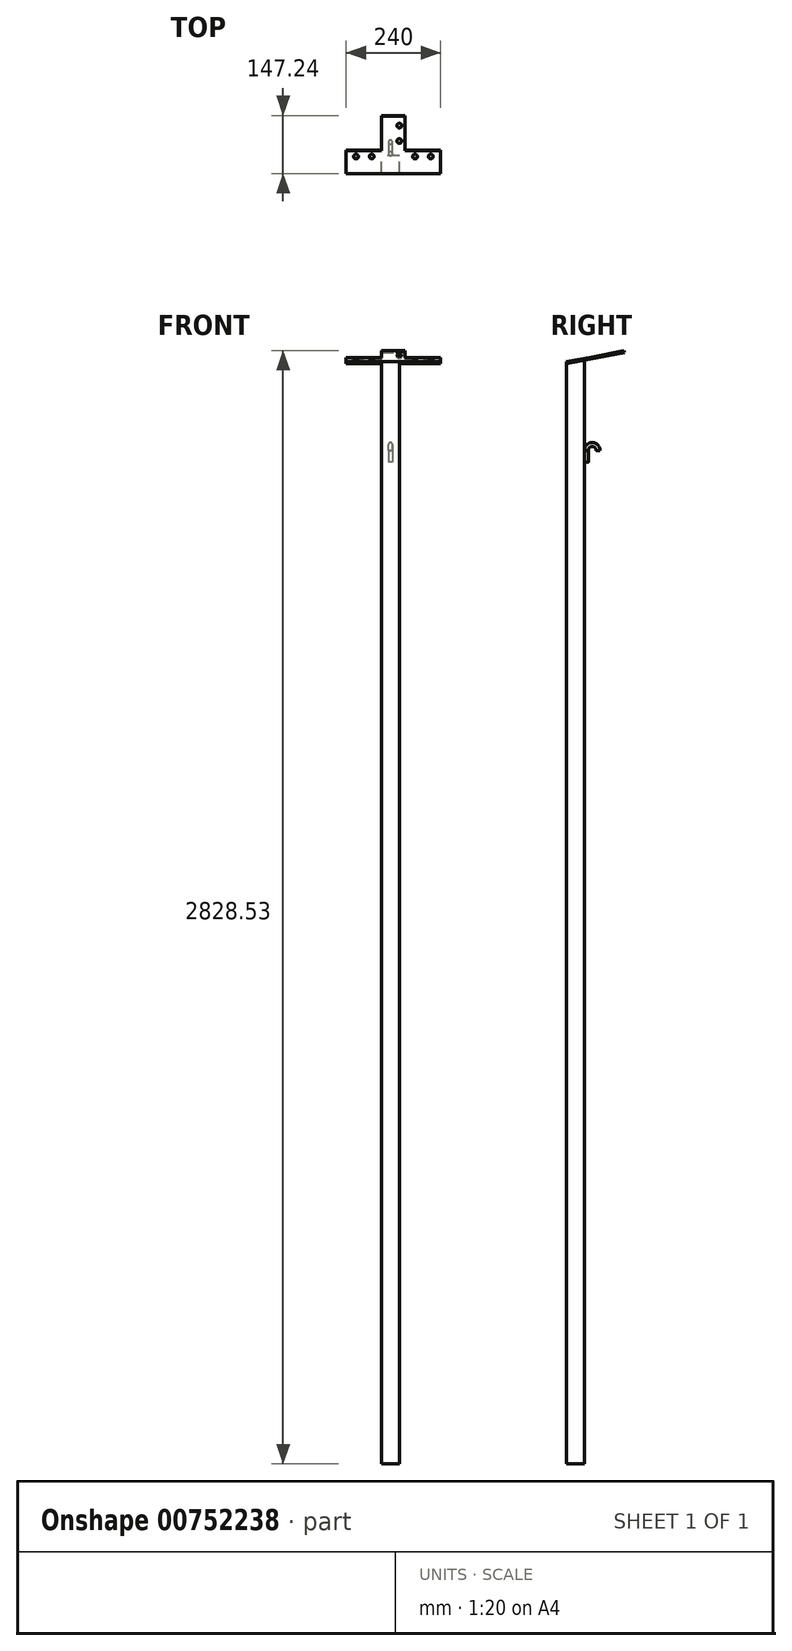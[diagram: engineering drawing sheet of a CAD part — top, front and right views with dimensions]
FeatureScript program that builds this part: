
annotation { "Feature Type Name" : "Feature", "Feature Type Description" : "" }
export const myFeature = defineFeature(function(context is Context, id is Id, definition is map)
    precondition{}
    {
        {
            var Q0;
            Q0=qCreatedBy(makeId("Top.planeOp"),FACE);
            var sketch = newSketch(context, id + "F0", { "sketchPlane" : qUnion([Q0])});
            skLineSegment(sketch, "E0.bottom", {"start": v(22.5, -22.5) * mm, "end": v(-22.5, -22.5) * mm});
            skLineSegment(sketch, "E0.top", {"start": v(22.5, 22.5) * mm, "end": v(-22.5, 22.5) * mm});
            skLineSegment(sketch, "E0.left", {"start": v(22.5, -22.5) * mm, "end": v(22.5, 22.5) * mm});
            skLineSegment(sketch, "E0.right", {"start": v(-22.5, -22.5) * mm, "end": v(-22.5, 22.5) * mm});
            skPoint(sketch, "E0.middle", {"position": v(0, 0) * mm});
            skSolve(sketch);
        }
        {
            var Q0;
            Q0=qSketchRegion(id+"F0",true);
            extrude(context, id + "F1", {"entities" : qUnion([Q0]), "depth" : 2795 * mm, "offsetDistance" : 25 * mm});
        }
        {
            var Q0;
            Q0=makeQuery(id+"F1.opExtrude","CAP_EDGE",EDGE,{"disambiguationData":[OSD([sQuery(id+"F0.wireOp",EDGE,"E0.bottom")])],"isStart":false});
            cPlane(context, id + "F2", {"entities" : qUnion([Q0]), "cplaneType" : CPlaneType.LINE_ANGLE, "offset" : 25 * mm, "angle" : 79 * degree, "width" : 150 * mm, "height" : 150 * mm});
        }
        {
            var Q0;
            Q0=qCreatedBy(id+"F2.planeOp",FACE);
            var sketch = newSketch(context, id + "F3", { "sketchPlane" : qUnion([Q0])});
            skLineSegment(sketch, "E1.bottom", {"start": v(-22.5, 511.22) * mm, "end": v(37.5, 511.22) * mm});
            skLineSegment(sketch, "E1.top", {"start": v(-22.5, 661.22) * mm, "end": v(37.5, 661.22) * mm});
            skLineSegment(sketch, "E1.left", {"start": v(-22.5, 511.22) * mm, "end": v(-22.5, 661.22) * mm});
            skLineSegment(sketch, "E1.right", {"start": v(37.5, 511.22) * mm, "end": v(37.5, 661.22) * mm});
            skLineSegment(sketch, "E2.bottom", {"start": v(37.5, 511.22) * mm, "end": v(127.5, 511.22) * mm});
            skLineSegment(sketch, "E2.top", {"start": v(37.5, 571.22) * mm, "end": v(127.5, 571.22) * mm});
            skLineSegment(sketch, "E2.left", {"start": v(37.5, 511.22) * mm, "end": v(37.5, 571.22) * mm});
            skLineSegment(sketch, "E2.right", {"start": v(127.5, 511.22) * mm, "end": v(127.5, 571.22) * mm});
            skLineSegment(sketch, "E3.bottom", {"start": v(22.5, 571.22) * mm, "end": v(-112.5, 571.22) * mm});
            skLineSegment(sketch, "E3.top", {"start": v(22.5, 511.22) * mm, "end": v(-112.5, 511.22) * mm});
            skLineSegment(sketch, "E3.left", {"start": v(22.5, 571.22) * mm, "end": v(22.5, 511.22) * mm});
            skLineSegment(sketch, "E3.right", {"start": v(-112.5, 571.22) * mm, "end": v(-112.5, 511.22) * mm});
            skSolve(sketch);
        }
        {
            var Q0;
            Q0=qSketchRegion(id+"F3",true);
            extrude(context, id + "F4", {"entities" : qUnion([Q0]), "depth" : 5 * mm, "offsetDistance" : 25 * mm});
        }
        {
            var Q0;
            Q0=makeQuery(id+"F1.opExtrude","SWEPT_FACE",FACE,{"disambiguationData":[OSD([sQuery(id+"F0.wireOp",EDGE,"E0.left")])]});
            var sketch = newSketch(context, id + "F5", { "sketchPlane" : qUnion([Q0])});
            skLineSegment(sketch, "E4", {"start": v(22.5, 2795) * mm, "end": v(22.5, 2803.75) * mm});
            skLineSegment(sketch, "E5", {"start": v(22.5, 2803.75) * mm, "end": v(-22.5, 2795) * mm});
            skLineSegment(sketch, "E6", {"start": v(-22.5, 2795) * mm, "end": v(22.5, 2795) * mm});
            skSolve(sketch);
        }
        {
            var Q0;
            Q0=qSketchRegion(id+"F5",true);
            extrude(context, id + "F6", {"entities" : qUnion([Q0]), "oppositeDirection" : true, "depth" : 45 * mm, "offsetDistance" : 25 * mm});
        }
        {
            var Q0;
            Q0=makeQuery(id+"F1.opExtrude","SWEPT_BODY",BODY,{"disambiguationData":[OSD([sQuery(id+"F0.wireOp",EDGE,"E0.bottom"),sQuery(id+"F0.wireOp",EDGE,"E0.top"),sQuery(id+"F0.wireOp",EDGE,"E0.left"),sQuery(id+"F0.wireOp",EDGE,"E0.right")])]});
            var Q1;
            Q1=makeQuery(id+"F6.opExtrude","SWEPT_BODY",BODY,{"disambiguationData":[OSD([sQuery(id+"F5.wireOp",EDGE,"E4"),sQuery(id+"F5.wireOp",EDGE,"E5"),sQuery(id+"F5.wireOp",EDGE,"E6")])]});
            var Q2;
            Q2=makeQuery(id+"F4.opExtrude","SWEPT_BODY",BODY,{"disambiguationData":[OSD([sQuery(id+"F3.wireOp",EDGE,"E1.bottom"),sQuery(id+"F3.wireOp",EDGE,"E1.top"),sQuery(id+"F3.wireOp",EDGE,"E1.left"),sQuery(id+"F3.wireOp",EDGE,"E1.right"),sQuery(id+"F3.wireOp",EDGE,"E2.bottom"),sQuery(id+"F3.wireOp",EDGE,"E2.top"),sQuery(id+"F3.wireOp",EDGE,"E2.right")])]});
            booleanBodies(context, id + "F7", {"operationType" : BooleanOperationType.UNION, "tools" : qUnion([Q0, Q1, Q2])});
        }
        {
            var Q0;
            Q0=makeQuery(id+"F7.opBoolean","MERGE",FACE,{"derivedFrom":[makeQuery(id+"F1.opExtrude","SWEPT_FACE",FACE,{"disambiguationData":[OSD([sQuery(id+"F0.wireOp",EDGE,"E0.right")])]}),makeQuery(id+"F4.opExtrude","SWEPT_FACE",FACE,{"disambiguationData":[OSD([sQuery(id+"F3.wireOp",EDGE,"E1.left")])]}),makeQuery(id+"F6.opExtrude","CAP_FACE",FACE,{"disambiguationData":[OSD([sQuery(id+"F5.wireOp",EDGE,"E4"),sQuery(id+"F5.wireOp",EDGE,"E5"),sQuery(id+"F5.wireOp",EDGE,"E6")])],"isStart":false})]});
            var sketch = newSketch(context, id + "F8", { "sketchPlane" : qUnion([Q0])});
            skLineSegment(sketch, "E7", {"start": v(9.37, 2795) * mm, "end": v(22.5, 2795) * mm});
            skLineSegment(sketch, "E8.bottom", {"start": v(22.5, 2795) * mm, "end": v(25.28, 2795) * mm});
            skLineSegment(sketch, "E8.top", {"start": v(22.5, 2800.7) * mm, "end": v(25.28, 2800.7) * mm});
            skLineSegment(sketch, "E8.left", {"start": v(22.5, 2795) * mm, "end": v(22.5, 2800.7) * mm});
            skLineSegment(sketch, "E8.right", {"start": v(25.28, 2795) * mm, "end": v(25.28, 2800.7) * mm});
            skSolve(sketch);
        }
        {
            var Q0;
            Q0=qSketchRegion(id+"F8",true);
            var Q1;
            Q1=makeQuery(id+"F4.opExtrude","SWEPT_FACE",FACE,{"disambiguationData":[OSD([sQuery(id+"F3.wireOp",EDGE,"E2.right")])]});
            var Q2;
            Q2=makeQuery(id+"F4.opExtrude","SWEPT_FACE",FACE,{"disambiguationData":[OSD([sQuery(id+"F3.wireOp",EDGE,"E3.right")])]});
            extrude(context, id + "F9", {"entities" : qUnion([Q0]), "operationType" : NewBodyOperationType.REMOVE, "endBound" : BoundingType.UP_TO_SURFACE, "oppositeDirection" : true, "depth" : 156.8 * mm, "endBoundEntityFace" : qUnion([Q1]), "offsetDistance" : 25 * mm, "hasSecondDirection" : true, "secondDirectionBound" : SecondDirectionBoundingType.UP_TO_SURFACE, "secondDirectionOppositeDirection" : false, "secondDirectionDepth" : 25 * mm, "secondDirectionBoundEntityFace" : qUnion([Q2])});
        }
        {
            var Q0;
            Q0=makeQuery(id+"F4.opExtrude","CAP_FACE",FACE,{"disambiguationData":[OSD([sQuery(id+"F3.wireOp",EDGE,"E1.bottom"),sQuery(id+"F3.wireOp",EDGE,"E1.top"),sQuery(id+"F3.wireOp",EDGE,"E1.left"),sQuery(id+"F3.wireOp",EDGE,"E1.right"),sQuery(id+"F3.wireOp",EDGE,"E2.bottom"),sQuery(id+"F3.wireOp",EDGE,"E2.top"),sQuery(id+"F3.wireOp",EDGE,"E2.right")])],"isStart":false});
            var sketch = newSketch(context, id + "F10", { "sketchPlane" : qUnion([Q0])});
            skLineSegment(sketch, "E9", {"start": v(127.5, 571.22) * mm, "end": v(102.5, 571.22) * mm});
            skLineSegment(sketch, "E10", {"start": v(102.5, 571.22) * mm, "end": v(102.5, 556.22) * mm});
            skLineSegment(sketch, "E11", {"start": v(102.5, 556.22) * mm, "end": v(62.5, 556.22) * mm});
            skCircle(sketch, "E12", {"center": v(102.5, 556.22) * mm, "radius": 6 * mm});
            skCircle(sketch, "E13", {"center": v(62.5, 556.22) * mm, "radius": 6 * mm});
            skLineSegment(sketch, "E14", {"start": v(37.5, 661.22) * mm, "end": v(37.5, 636.22) * mm});
            skLineSegment(sketch, "E15", {"start": v(37.5, 636.22) * mm, "end": v(22.5, 636.22) * mm});
            skLineSegment(sketch, "E16", {"start": v(22.5, 636.22) * mm, "end": v(22.5, 596.22) * mm});
            skCircle(sketch, "E17", {"center": v(22.5, 636.22) * mm, "radius": 6 * mm});
            skCircle(sketch, "E18", {"center": v(22.5, 596.22) * mm, "radius": 6 * mm});
            skLineSegment(sketch, "E19", {"start": v(7.5, 661.22) * mm, "end": v(7.5, 641.46) * mm});
            skCircle(sketch, "E20.MirrorC", {"center": v(-47.5, 556.22) * mm, "radius": 6 * mm});
            skCircle(sketch, "E21.MirrorC", {"center": v(-87.5, 556.22) * mm, "radius": 6 * mm});
            skLineSegment(sketch, "E22", {"start": v(-22.5, 661.22) * mm, "end": v(37.5, 661.22) * mm});
            skSolve(sketch);
        }
        {
            var Q0;
            Q0=qSketchRegion(id+"F10",true);
            var Q1;
            Q1=makeQuery(id+"F4.opExtrude","CAP_FACE",FACE,{"disambiguationData":[OSD([sQuery(id+"F3.wireOp",EDGE,"E1.bottom"),sQuery(id+"F3.wireOp",EDGE,"E1.top"),sQuery(id+"F3.wireOp",EDGE,"E1.left"),sQuery(id+"F3.wireOp",EDGE,"E1.right"),sQuery(id+"F3.wireOp",EDGE,"E2.bottom"),sQuery(id+"F3.wireOp",EDGE,"E2.top"),sQuery(id+"F3.wireOp",EDGE,"E2.right")])],"isStart":true});
            extrude(context, id + "F11", {"entities" : qUnion([Q0]), "operationType" : NewBodyOperationType.REMOVE, "endBound" : BoundingType.UP_TO_SURFACE, "oppositeDirection" : true, "depth" : 25 * mm, "endBoundEntityFace" : qUnion([Q1]), "offsetDistance" : 25 * mm});
        }
        {
            var Q0;
            Q0=qCreatedBy(makeId("Top.planeOp"),FACE);
            cPlane(context, id + "F12", {"entities" : qUnion([Q0]), "cplaneType" : CPlaneType.OFFSET, "offset" : 2545 * mm, "width" : 150 * mm, "height" : 150 * mm});
        }
        {
            var Q0;
            Q0=qCreatedBy(makeId("Right.planeOp"),FACE);
            var sketch = newSketch(context, id + "F13", { "sketchPlane" : qUnion([Q0])});
            skLineSegment(sketch, "E23", {"start": v(27.5, 2545) * mm, "end": v(27.5, 2575) * mm});
            skLineSegment(sketch, "E24", {"start": v(27.5, 2575) * mm, "end": v(57.5, 2575) * mm});
            skArc(sketch, "E25", {"start": v(57.5, 2575) * mm, "mid": v(42.5, 2590) * mm, "end": v(27.5, 2575) * mm});
            skLineSegment(sketch, "E26", {"start": v(27.5, 2545) * mm, "end": v(22.5, 2545) * mm});
            skSolve(sketch);
        }
        {
            var Q0;
            Q0=qCreatedBy(id+"F12.planeOp",FACE);
            var sketch = newSketch(context, id + "F14", { "sketchPlane" : qUnion([Q0])});
            skCircle(sketch, "E27", {"center": v(0, 27.5) * mm, "radius": 5 * mm});
            skLineSegment(sketch, "E28", {"start": v(0, 27.5) * mm, "end": v(0, 22.5) * mm});
            skLineSegment(sketch, "E29", {"start": v(0, 22.5) * mm, "end": v(-5, 22.5) * mm});
            skLineSegment(sketch, "E30", {"start": v(0, 27.5) * mm, "end": v(-5, 27.5) * mm});
            skLineSegment(sketch, "E31", {"start": v(-5, 27.5) * mm, "end": v(-5, 22.5) * mm});
            skLineSegment(sketch, "E32", {"start": v(0, 27.5) * mm, "end": v(5, 27.5) * mm});
            skLineSegment(sketch, "E33", {"start": v(5, 27.5) * mm, "end": v(5, 22.5) * mm});
            skLineSegment(sketch, "E34", {"start": v(0, 22.5) * mm, "end": v(5, 22.5) * mm});
            skSolve(sketch);
        }
        {
            var Q0;
            Q0 = qSketchRegion(id + "F14", true);
            extrude(context, id + "F15", {"entities" : qUnion([Q0]), "operationType" : NewBodyOperationType.ADD, "depth" : 30 * mm, "offsetDistance" : 25 * mm});
        }
        {
            var Q0;
            Q0=makeQuery(id+"F15.opExtrude","CAP_FACE",FACE,{"disambiguationData":[OSD([sQuery(id+"F14.wireOp",EDGE,"E27"),sQuery(id+"F14.wireOp",EDGE,"E29"),sQuery(id+"F14.wireOp",EDGE,"E31"),sQuery(id+"F14.wireOp",EDGE,"E33"),sQuery(id+"F14.wireOp",EDGE,"E34")])],"isStart":false});
            var sketch = newSketch(context, id + "F16", { "sketchPlane" : qUnion([Q0])});
            skArc(sketch, "E35.0", {"start": v(5, 27.5) * mm, "mid": v(0, 32.5) * mm, "end": v(-5, 27.5) * mm});
            skLineSegment(sketch, "E36", {"start": v(0, 27.5) * mm, "end": v(5, 27.5) * mm});
            skArc(sketch, "E37.MirrorCS", {"start": v(5, 27.5) * mm, "mid": v(0, 22.5) * mm, "end": v(-5, 27.5) * mm});
            skSolve(sketch);
        }
        {
            var Q0;
            {var subQ0=sQuery(id+"F16.wireOp",EDGE,"E35.0");Q0=makeQuery(id+"F16.imprint","IMPRINT",FACE,{"disambiguationData":[TD([[makeQuery(id+"F16.imprint","IMPRINT",EDGE,{"derivedFrom":subQ0}),1.0]])]});}
            var Q1;
            Q1=sQuery(id+"F13.wireOp",EDGE,"E25");
            sweep(context, id + "F17", {"operationType" : NewBodyOperationType.ADD, "profiles" : qUnion([Q0]), "path" : qUnion([Q1])});
        }
    });
